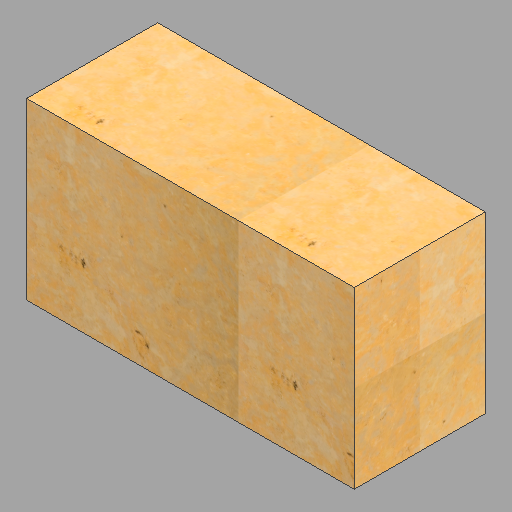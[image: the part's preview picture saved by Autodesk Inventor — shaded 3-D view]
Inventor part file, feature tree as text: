
AUTODESK INVENTOR PART (.ipt)
format: ipt  version: 2023 (Build 270158000, 158)  size: 398,336 bytes
history: native  units: in
note: dims shown in document units (in); Inventor stores cm internally (conversion verified against a paired STEP export)
features: extrude x1, sketch x1
ambient origin geometry x8: Origin, YZ Plane, XZ Plane, XY Plane, X Axis, Y Axis, Z Axis, Center Point
bodies: Solid1 (feature_tree)
feature tree (2):
  extrude  "Extrusion1"  Depth=18.0in
  sketch  "Sketch1"  dims[d0=24.0in d1=18.0in d2=45.0in d3=0.0in]
